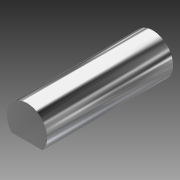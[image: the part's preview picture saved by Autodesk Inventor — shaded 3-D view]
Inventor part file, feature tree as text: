
AUTODESK INVENTOR PART (.ipt)
format: ipt  version: 2014 (Build 180170000, 170)  size: 87,552 bytes
history: native  units: in
note: dims shown in document units (in); Inventor stores cm internally (conversion verified against a paired STEP export)
features: extrude x2, sketch x2
ambient origin geometry x8: Origin, YZ Plane, XZ Plane, XY Plane, X Axis, Y Axis, Z Axis, Center Point
bodies: Solid1 (feature_tree)
feature tree (4):
  extrude  "Extrusion1"  Depth=0.475in TaperAngle=0.0deg
  extrude  "Extrusion2"  Depth=0.26in TaperAngle=0.0deg
  sketch  "Sketch1"  dims[d0=0.152in d1=0.475in d2=0.0in]
  sketch  "Sketch2"  dims[d3=0.125in d4=0.26in d5=0.0in]
